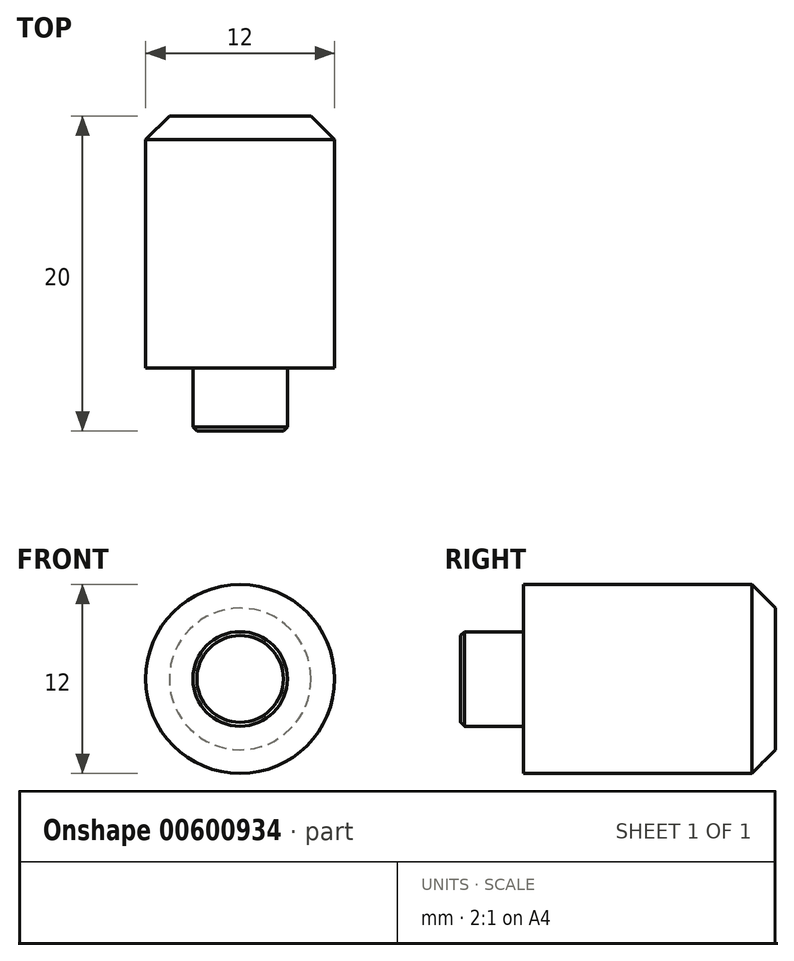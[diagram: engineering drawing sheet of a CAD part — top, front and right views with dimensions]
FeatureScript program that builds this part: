
annotation { "Feature Type Name" : "Feature", "Feature Type Description" : "" }
export const myFeature = defineFeature(function(context is Context, id is Id, definition is map)
    precondition{}
    {
        {
            var Q0;
            Q0=qCreatedBy(makeId("Front.planeOp"),FACE);
            var sketch = newSketch(context, id + "F0", { "sketchPlane" : qUnion([Q0])});
            skCircle(sketch, "E0", {"center": v(0, 0) * mm, "radius": 6 * mm});
            skSolve(sketch);
        }
        {
            var Q0;
            Q0=makeQuery(id+"F0.imprint","IMPRINT",FACE,{"disambiguationData":[TD([[makeQuery(id+"F0.imprint","IMPRINT",EDGE,{"derivedFrom":sQuery(id+"F0.wireOp",EDGE,"E0")}),1.0]])]});
            extrude(context, id + "F1", {"entities" : qUnion([Q0]), "oppositeDirection" : true, "depth" : 16 * mm});
        }
        {
            var Q0;
            Q0=makeQuery(id+"F1.opExtrude","CAP_FACE",FACE,{"disambiguationData":[OSD([sQuery(id+"F0.wireOp",EDGE,"E0")])],"isStart":true});
            var sketch = newSketch(context, id + "F2", { "sketchPlane" : qUnion([Q0])});
            skCircle(sketch, "E1", {"center": v(0, 0) * mm, "radius": 3 * mm});
            skSolve(sketch);
        }
        {
            var Q0;
            Q0=makeQuery(id+"F2.imprint","IMPRINT",FACE,{"disambiguationData":[TD([[makeQuery(id+"F2.imprint","IMPRINT",EDGE,{"derivedFrom":sQuery(id+"F2.wireOp",EDGE,"E1")}),1.0]])]});
            extrude(context, id + "F3", {"entities" : qUnion([Q0]), "operationType" : NewBodyOperationType.ADD, "depth" : 4 * mm});
        }
        {
            var Q0;
            Q0=makeQuery(id+"F3.opExtrude","CAP_EDGE",EDGE,{"disambiguationData":[OSD([sQuery(id+"F2.wireOp",EDGE,"E1")])],"isStart":false});
            chamfer(context, id + "F4", {"entities" : qUnion([Q0]), "width" : 0.25 * mm, "tangentPropagation" : true});
        }
        {
            var Q0;
            Q0=makeQuery(id+"F1.opExtrude","CAP_EDGE",EDGE,{"disambiguationData":[OSD([sQuery(id+"F0.wireOp",EDGE,"E0")])],"isStart":false});
            chamfer(context, id + "F5", {"entities" : qUnion([Q0]), "width" : 1.5 * mm, "tangentPropagation" : true});
        }
    });
